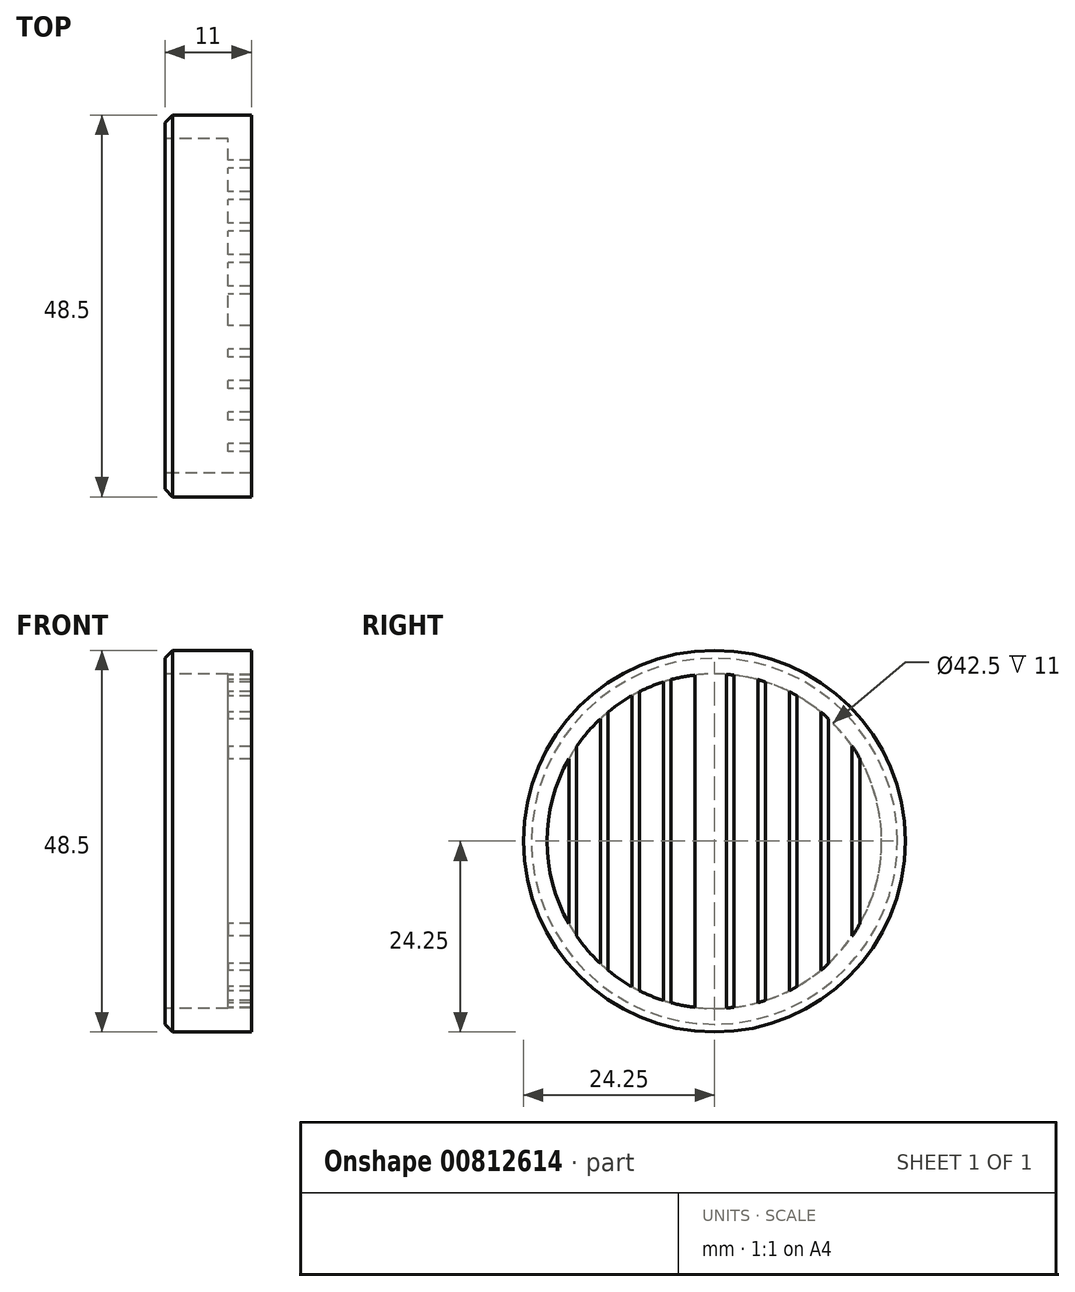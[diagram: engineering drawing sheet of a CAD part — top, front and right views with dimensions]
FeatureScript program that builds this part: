
annotation { "Feature Type Name" : "Feature", "Feature Type Description" : "" }
export const myFeature = defineFeature(function(context is Context, id is Id, definition is map)
    precondition{}
    {
        {
            var Q0;
            Q0=qCreatedBy(makeId("Right.planeOp"),FACE);
            var sketch = newSketch(context, id + "F0", { "sketchPlane" : qUnion([Q0])});
            skCircle(sketch, "E0", {"center": v(0, 0) * mm, "radius": 24.25 * mm});
            skCircle(sketch, "E1", {"center": v(0, 0) * mm, "radius": 21.25 * mm});
            skSolve(sketch);
        }
        {
            var Q0;
            Q0 = qSketchRegion(id + "F0", true);
            extrude(context, id + "F1", {"entities" : qUnion([Q0]), "depth" : 8 * mm, "offsetDistance" : 25 * mm});
        }
        {
            var Q0;
            Q0=makeQuery(id+"F1.opExtrude","CAP_FACE",FACE,{"disambiguationData":[OSD([sQuery(id+"F0.wireOp",EDGE,"E0"),sQuery(id+"F0.wireOp",EDGE,"E1")])],"isStart":false});
            var sketch = newSketch(context, id + "F2", { "sketchPlane" : qUnion([Q0])});
            skCircle(sketch, "E2.0", {"center": v(0, 0) * mm, "radius": 24.25 * mm});
            skSolve(sketch);
        }
        {
            var Q0;
            Q0 = qSketchRegion(id + "F2", true);
            extrude(context, id + "F3", {"entities" : qUnion([Q0]), "operationType" : NewBodyOperationType.ADD, "depth" : 3 * mm, "offsetDistance" : 25 * mm});
        }
        {
            var Q0;
            Q0=makeQuery(id+"F3.opExtrude","CAP_FACE",FACE,{"disambiguationData":[OSD([sQuery(id+"F2.wireOp",EDGE,"E2.0")])],"isStart":false});
            var sketch = newSketch(context, id + "F4", { "sketchPlane" : qUnion([Q0])});
            skCircle(sketch, "E3.0", {"center": v(0, 0) * mm, "radius": 21.25 * mm});
            skLineSegment(sketch, "E4.bottom", {"start": v(-1.5, 24.25) * mm, "end": v(1.5, 24.25) * mm});
            skLineSegment(sketch, "E4.top", {"start": v(-1.5, -24.25) * mm, "end": v(1.5, -24.25) * mm});
            skLineSegment(sketch, "E4.left", {"start": v(-1.5, 24.25) * mm, "end": v(-1.5, -24.25) * mm});
            skLineSegment(sketch, "E4.right", {"start": v(1.5, 24.25) * mm, "end": v(1.5, -24.25) * mm});
            skLineSegment(sketch, "E5.1.0.0", {"start": v(2.5, 24.25) * mm, "end": v(2.5, -24.25) * mm});
            skLineSegment(sketch, "E5.1.0.1", {"start": v(5.5, 24.25) * mm, "end": v(5.5, -24.25) * mm});
            skLineSegment(sketch, "E5.1.0.2", {"start": v(2.5, 24.25) * mm, "end": v(5.5, 24.25) * mm});
            skLineSegment(sketch, "E5.1.0.3", {"start": v(2.5, -24.25) * mm, "end": v(5.5, -24.25) * mm});
            skLineSegment(sketch, "E5.2.0.0", {"start": v(6.5, 24.25) * mm, "end": v(6.5, -24.25) * mm});
            skLineSegment(sketch, "E5.2.0.1", {"start": v(9.5, 24.25) * mm, "end": v(9.5, -24.25) * mm});
            skLineSegment(sketch, "E5.2.0.2", {"start": v(6.5, 24.25) * mm, "end": v(9.5, 24.25) * mm});
            skLineSegment(sketch, "E5.2.0.3", {"start": v(6.5, -24.25) * mm, "end": v(9.5, -24.25) * mm});
            skLineSegment(sketch, "E5.3.0.0", {"start": v(10.5, 24.25) * mm, "end": v(10.5, -24.25) * mm});
            skLineSegment(sketch, "E5.3.0.1", {"start": v(13.5, 24.25) * mm, "end": v(13.5, -24.25) * mm});
            skLineSegment(sketch, "E5.3.0.2", {"start": v(10.5, 24.25) * mm, "end": v(13.5, 24.25) * mm});
            skLineSegment(sketch, "E5.3.0.3", {"start": v(10.5, -24.25) * mm, "end": v(13.5, -24.25) * mm});
            skLineSegment(sketch, "E5.4.0.0", {"start": v(14.5, 24.25) * mm, "end": v(14.5, -24.25) * mm});
            skLineSegment(sketch, "E5.4.0.1", {"start": v(17.5, 24.25) * mm, "end": v(17.5, -24.25) * mm});
            skLineSegment(sketch, "E5.4.0.2", {"start": v(14.5, 24.25) * mm, "end": v(17.5, 24.25) * mm});
            skLineSegment(sketch, "E5.4.0.3", {"start": v(14.5, -24.25) * mm, "end": v(17.5, -24.25) * mm});
            skLineSegment(sketch, "E5.5.0.0", {"start": v(18.5, 24.25) * mm, "end": v(18.5, -24.25) * mm});
            skLineSegment(sketch, "E5.5.0.1", {"start": v(21.5, 24.25) * mm, "end": v(21.5, -24.25) * mm});
            skLineSegment(sketch, "E5.5.0.2", {"start": v(18.5, 24.25) * mm, "end": v(21.5, 24.25) * mm});
            skLineSegment(sketch, "E5.5.0.3", {"start": v(18.5, -24.25) * mm, "end": v(21.5, -24.25) * mm});
            skLineSegment(sketch, "E5.6.0.0", {"start": v(22.5, 24.25) * mm, "end": v(22.5, -24.25) * mm});
            skLineSegment(sketch, "E5.6.0.1", {"start": v(25.5, 24.25) * mm, "end": v(25.5, -24.25) * mm});
            skLineSegment(sketch, "E5.6.0.2", {"start": v(22.5, 24.25) * mm, "end": v(25.5, 24.25) * mm});
            skLineSegment(sketch, "E5.6.0.3", {"start": v(22.5, -24.25) * mm, "end": v(25.5, -24.25) * mm});
            skLineSegment(sketch, "E5.7.0.0", {"start": v(26.5, 24.25) * mm, "end": v(26.5, -24.25) * mm});
            skLineSegment(sketch, "E5.7.0.1", {"start": v(29.5, 24.25) * mm, "end": v(29.5, -24.25) * mm});
            skLineSegment(sketch, "E5.7.0.2", {"start": v(26.5, 24.25) * mm, "end": v(29.5, 24.25) * mm});
            skLineSegment(sketch, "E5.7.0.3", {"start": v(26.5, -24.25) * mm, "end": v(29.5, -24.25) * mm});
            skLineSegment(sketch, "E5.direction1", {"start": v(-1.5, -24.25) * mm, "end": v(2.5, -24.25) * mm, "construction": true});
            skLineSegment(sketch, "E6.1.0.0", {"start": v(-5.5, 24.25) * mm, "end": v(-5.5, -24.25) * mm});
            skLineSegment(sketch, "E6.1.0.1", {"start": v(-5.5, 24.25) * mm, "end": v(-2.5, 24.25) * mm});
            skLineSegment(sketch, "E6.1.0.2", {"start": v(-2.5, 24.25) * mm, "end": v(-2.5, -24.25) * mm});
            skLineSegment(sketch, "E6.1.0.3", {"start": v(-5.5, -24.25) * mm, "end": v(-1.5, -24.25) * mm, "construction": true});
            skLineSegment(sketch, "E6.2.0.0", {"start": v(-9.5, 24.25) * mm, "end": v(-9.5, -24.25) * mm});
            skLineSegment(sketch, "E6.2.0.1", {"start": v(-9.5, 24.25) * mm, "end": v(-6.5, 24.25) * mm});
            skLineSegment(sketch, "E6.2.0.2", {"start": v(-6.5, 24.25) * mm, "end": v(-6.5, -24.25) * mm});
            skLineSegment(sketch, "E6.2.0.3", {"start": v(-9.5, -24.25) * mm, "end": v(-5.5, -24.25) * mm, "construction": true});
            skLineSegment(sketch, "E6.3.0.0", {"start": v(-13.5, 24.25) * mm, "end": v(-13.5, -24.25) * mm});
            skLineSegment(sketch, "E6.3.0.1", {"start": v(-13.5, 24.25) * mm, "end": v(-10.5, 24.25) * mm});
            skLineSegment(sketch, "E6.3.0.2", {"start": v(-10.5, 24.25) * mm, "end": v(-10.5, -24.25) * mm});
            skLineSegment(sketch, "E6.3.0.3", {"start": v(-13.5, -24.25) * mm, "end": v(-9.5, -24.25) * mm, "construction": true});
            skLineSegment(sketch, "E6.4.0.0", {"start": v(-17.5, 24.25) * mm, "end": v(-17.5, -24.25) * mm});
            skLineSegment(sketch, "E6.4.0.1", {"start": v(-17.5, 24.25) * mm, "end": v(-14.5, 24.25) * mm});
            skLineSegment(sketch, "E6.4.0.2", {"start": v(-14.5, 24.25) * mm, "end": v(-14.5, -24.25) * mm});
            skLineSegment(sketch, "E6.4.0.3", {"start": v(-17.5, -24.25) * mm, "end": v(-13.5, -24.25) * mm, "construction": true});
            skLineSegment(sketch, "E6.5.0.0", {"start": v(-21.5, 24.25) * mm, "end": v(-21.5, -24.25) * mm});
            skLineSegment(sketch, "E6.5.0.1", {"start": v(-21.5, 24.25) * mm, "end": v(-18.5, 24.25) * mm});
            skLineSegment(sketch, "E6.5.0.2", {"start": v(-18.5, 24.25) * mm, "end": v(-18.5, -24.25) * mm});
            skLineSegment(sketch, "E6.5.0.3", {"start": v(-21.5, -24.25) * mm, "end": v(-17.5, -24.25) * mm, "construction": true});
            skLineSegment(sketch, "E6.6.0.0", {"start": v(-25.5, 24.25) * mm, "end": v(-25.5, -24.25) * mm});
            skLineSegment(sketch, "E6.6.0.1", {"start": v(-25.5, 24.25) * mm, "end": v(-22.5, 24.25) * mm});
            skLineSegment(sketch, "E6.6.0.2", {"start": v(-22.5, 24.25) * mm, "end": v(-22.5, -24.25) * mm});
            skLineSegment(sketch, "E6.6.0.3", {"start": v(-25.5, -24.25) * mm, "end": v(-21.5, -24.25) * mm, "construction": true});
            skLineSegment(sketch, "E6.7.0.0", {"start": v(-29.5, 24.25) * mm, "end": v(-29.5, -24.25) * mm});
            skLineSegment(sketch, "E6.7.0.1", {"start": v(-29.5, 24.25) * mm, "end": v(-26.5, 24.25) * mm});
            skLineSegment(sketch, "E6.7.0.2", {"start": v(-26.5, 24.25) * mm, "end": v(-26.5, -24.25) * mm});
            skLineSegment(sketch, "E6.7.0.3", {"start": v(-29.5, -24.25) * mm, "end": v(-25.5, -24.25) * mm, "construction": true});
            skLineSegment(sketch, "E6.direction1", {"start": v(-1.5, -24.25) * mm, "end": v(-5.5, -24.25) * mm, "construction": true});
            skSolve(sketch);
        }
        {
            var Q0;
            {var subQ0=sQuery(id+"F4.wireOp",EDGE,"E4.right");var subQ1=sQuery(id+"F4.wireOp",EDGE,"E3.0");var subQ2=makeQuery(id+"F4.imprint","INTERSECT",VERTEX,{"disambiguationData":[OD(1.0)],"derivedFrom":[subQ1,subQ0]});Q0=makeQuery(id+"F4.imprint","IMPRINT",FACE,{"disambiguationData":[TD([[makeQuery(id+"F4.imprint","IMPRINT",EDGE,{"disambiguationData":[TD([[subQ2,-1.0]])],"derivedFrom":subQ1}),1.0]])]});}
            var Q1;
            {var subQ0=sQuery(id+"F4.wireOp",EDGE,"E5.1.0.0");var subQ1=sQuery(id+"F4.wireOp",EDGE,"E3.0");var subQ2=makeQuery(id+"F4.imprint","INTERSECT",VERTEX,{"disambiguationData":[OD(0.0)],"derivedFrom":[subQ1,subQ0]});Q1=makeQuery(id+"F4.imprint","IMPRINT",FACE,{"disambiguationData":[TD([[makeQuery(id+"F4.imprint","IMPRINT",EDGE,{"disambiguationData":[TD([[subQ2,-1.0]])],"derivedFrom":subQ1}),1.0]])]});}
            var Q2;
            {var subQ0=sQuery(id+"F4.wireOp",EDGE,"E5.2.0.0");var subQ1=sQuery(id+"F4.wireOp",EDGE,"E3.0");var subQ2=makeQuery(id+"F4.imprint","INTERSECT",VERTEX,{"disambiguationData":[OD(0.0)],"derivedFrom":[subQ1,subQ0]});Q2=makeQuery(id+"F4.imprint","IMPRINT",FACE,{"disambiguationData":[TD([[makeQuery(id+"F4.imprint","IMPRINT",EDGE,{"disambiguationData":[TD([[subQ2,-1.0]])],"derivedFrom":subQ1}),1.0]])]});}
            var Q3;
            {var subQ0=sQuery(id+"F4.wireOp",EDGE,"E5.3.0.0");var subQ1=sQuery(id+"F4.wireOp",EDGE,"E3.0");var subQ2=makeQuery(id+"F4.imprint","INTERSECT",VERTEX,{"disambiguationData":[OD(0.0)],"derivedFrom":[subQ1,subQ0]});Q3=makeQuery(id+"F4.imprint","IMPRINT",FACE,{"disambiguationData":[TD([[makeQuery(id+"F4.imprint","IMPRINT",EDGE,{"disambiguationData":[TD([[subQ2,-1.0]])],"derivedFrom":subQ1}),1.0]])]});}
            var Q4;
            {var subQ0=sQuery(id+"F4.wireOp",EDGE,"E5.4.0.0");var subQ1=sQuery(id+"F4.wireOp",EDGE,"E3.0");var subQ2=makeQuery(id+"F4.imprint","INTERSECT",VERTEX,{"disambiguationData":[OD(0.0)],"derivedFrom":[subQ1,subQ0]});Q4=makeQuery(id+"F4.imprint","IMPRINT",FACE,{"disambiguationData":[TD([[makeQuery(id+"F4.imprint","IMPRINT",EDGE,{"disambiguationData":[TD([[subQ2,-1.0]])],"derivedFrom":subQ1}),1.0]])]});}
            var Q5;
            {var subQ0=sQuery(id+"F4.wireOp",EDGE,"E5.5.0.0");var subQ1=sQuery(id+"F4.wireOp",EDGE,"E3.0");var subQ2=makeQuery(id+"F4.imprint","INTERSECT",VERTEX,{"disambiguationData":[OD(0.0)],"derivedFrom":[subQ1,subQ0]});Q5=makeQuery(id+"F4.imprint","IMPRINT",FACE,{"disambiguationData":[TD([[makeQuery(id+"F4.imprint","IMPRINT",EDGE,{"disambiguationData":[TD([[subQ2,-1.0]])],"derivedFrom":subQ1}),1.0]])]});}
            var Q6;
            {var subQ0=sQuery(id+"F4.wireOp",EDGE,"E6.1.0.2");var subQ1=sQuery(id+"F4.wireOp",EDGE,"E3.0");var subQ2=makeQuery(id+"F4.imprint","INTERSECT",VERTEX,{"disambiguationData":[OD(0.0)],"derivedFrom":[subQ1,subQ0]});Q6=makeQuery(id+"F4.imprint","IMPRINT",FACE,{"disambiguationData":[TD([[makeQuery(id+"F4.imprint","IMPRINT",EDGE,{"disambiguationData":[TD([[subQ2,-1.0]])],"derivedFrom":subQ1}),1.0]])]});}
            var Q7;
            {var subQ0=sQuery(id+"F4.wireOp",EDGE,"E6.2.0.2");var subQ1=sQuery(id+"F4.wireOp",EDGE,"E3.0");var subQ2=makeQuery(id+"F4.imprint","INTERSECT",VERTEX,{"disambiguationData":[OD(0.0)],"derivedFrom":[subQ1,subQ0]});Q7=makeQuery(id+"F4.imprint","IMPRINT",FACE,{"disambiguationData":[TD([[makeQuery(id+"F4.imprint","IMPRINT",EDGE,{"disambiguationData":[TD([[subQ2,-1.0]])],"derivedFrom":subQ1}),1.0]])]});}
            var Q8;
            {var subQ0=sQuery(id+"F4.wireOp",EDGE,"E6.3.0.2");var subQ1=sQuery(id+"F4.wireOp",EDGE,"E3.0");var subQ2=makeQuery(id+"F4.imprint","INTERSECT",VERTEX,{"disambiguationData":[OD(0.0)],"derivedFrom":[subQ1,subQ0]});Q8=makeQuery(id+"F4.imprint","IMPRINT",FACE,{"disambiguationData":[TD([[makeQuery(id+"F4.imprint","IMPRINT",EDGE,{"disambiguationData":[TD([[subQ2,-1.0]])],"derivedFrom":subQ1}),1.0]])]});}
            var Q9;
            {var subQ0=sQuery(id+"F4.wireOp",EDGE,"E6.4.0.2");var subQ1=sQuery(id+"F4.wireOp",EDGE,"E3.0");var subQ2=makeQuery(id+"F4.imprint","INTERSECT",VERTEX,{"disambiguationData":[OD(0.0)],"derivedFrom":[subQ1,subQ0]});Q9=makeQuery(id+"F4.imprint","IMPRINT",FACE,{"disambiguationData":[TD([[makeQuery(id+"F4.imprint","IMPRINT",EDGE,{"disambiguationData":[TD([[subQ2,-1.0]])],"derivedFrom":subQ1}),1.0]])]});}
            var Q10;
            {var subQ0=sQuery(id+"F4.wireOp",EDGE,"E6.5.0.2");var subQ1=sQuery(id+"F4.wireOp",EDGE,"E3.0");var subQ2=makeQuery(id+"F4.imprint","INTERSECT",VERTEX,{"disambiguationData":[OD(0.0)],"derivedFrom":[subQ1,subQ0]});Q10=makeQuery(id+"F4.imprint","IMPRINT",FACE,{"disambiguationData":[TD([[makeQuery(id+"F4.imprint","IMPRINT",EDGE,{"disambiguationData":[TD([[subQ2,-1.0]])],"derivedFrom":subQ1}),1.0]])]});}
            extrude(context, id + "F5", {"entities" : qUnion([Q0, Q1, Q2, Q3, Q4, Q5, Q6, Q7, Q8, Q9, Q10]), "operationType" : NewBodyOperationType.REMOVE, "depth" : 10 * mm, "offsetDistance" : 25 * mm, "hasSecondDirection" : true, "secondDirectionOppositeDirection" : true, "secondDirectionDepth" : 25 * mm});
        }
        {
            var Q0;
            Q0=makeQuery(id+"F1.opExtrude","CAP_EDGE",EDGE,{"disambiguationData":[OSD([sQuery(id+"F0.wireOp",EDGE,"E0")])],"isStart":true});
            chamfer(context, id + "F6", {"entities" : qUnion([Q0]), "width" : 1 * mm, "tangentPropagation" : true});
        }
    });
